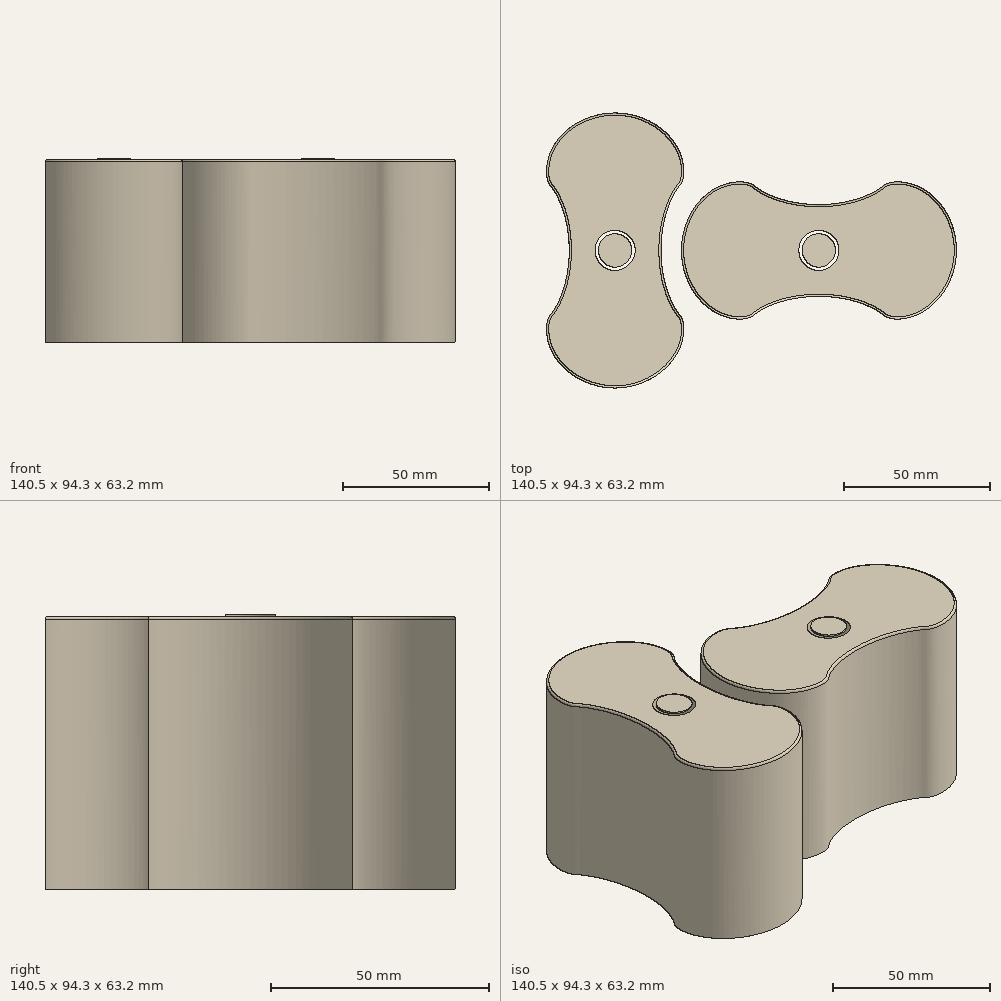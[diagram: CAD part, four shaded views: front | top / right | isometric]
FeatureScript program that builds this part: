
annotation { "Feature Type Name" : "Feature", "Feature Type Description" : "" }
export const myFeature = defineFeature(function(context is Context, id is Id, definition is map)
    precondition{}
    {
        {
            var Q0;
            Q0=qCreatedBy(makeId("Top.planeOp"),FACE);
            var sketch = newSketch(context, id + "F0", { "sketchPlane" : qUnion([Q0])});
            skCircle(sketch, "E0", {"center": v(0, 0) * mm, "radius": 31.43 * mm, "construction": true});
            skCircle(sketch, "E1", {"center": v(0, 39.3) * mm, "radius": 7.86 * mm, "construction": true});
            skLineSegment(sketch, "E2", {"start": v(0, 47.15) * mm, "end": v(0, 39.3) * mm, "construction": true});
            skLineSegment(sketch, "E3", {"start": v(0, 0) * mm, "end": v(-23.57, 0) * mm, "construction": true});
            skCircle(sketch, "E4", {"center": v(-23.57, 0) * mm, "radius": 7.86 * mm, "construction": true});
            skLineSegment(sketch, "E5", {"start": v(0, 0) * mm, "end": v(0, 47.15) * mm, "construction": true});
            skCircle(sketch, "E6", {"center": v(0, 0) * mm, "radius": 47.15 * mm, "construction": true});
            skLineSegment(sketch, "E7", {"start": v(0, 0) * mm, "end": v(-22.23, 22.23) * mm, "construction": true});
            skLineSegment(sketch, "E8", {"start": v(0, 0) * mm, "end": v(0, -47.15) * mm, "construction": true});
            skLineSegment(sketch, "E9", {"start": v(0, 0) * mm, "end": v(-22.23, -22.23) * mm, "construction": true});
            skCircle(sketch, "E10", {"center": v(0, -39.3) * mm, "radius": 7.86 * mm, "construction": true});
            skCircle(sketch, "E11", {"center": v(-15.04, 36.3) * mm, "radius": 7.86 * mm, "construction": true});
            skCircle(sketch, "E12", {"center": v(-21.78, 9.02) * mm, "radius": 7.86 * mm, "construction": true});
            skLineSegment(sketch, "E13", {"start": v(-15.04, 36.3) * mm, "end": v(0, 0) * mm, "construction": true});
            skLineSegment(sketch, "E14", {"start": v(0, 0) * mm, "end": v(-21.78, 9.02) * mm, "construction": true});
            skLineSegment(sketch, "E15", {"start": v(-21.78, 9.02) * mm, "end": v(-18.77, 16.28) * mm, "construction": true});
            skLineSegment(sketch, "E16", {"start": v(-15.04, 36.3) * mm, "end": v(-22.3, 33.3) * mm, "construction": true});
            skPoint(sketch, "E17", {"position": v(-15.72, 0) * mm});
            skCircle(sketch, "E18", {"center": v(-21.78, -9.02) * mm, "radius": 7.86 * mm, "construction": true});
            skCircle(sketch, "E19", {"center": v(-15.04, -36.3) * mm, "radius": 7.86 * mm, "construction": true});
            skLineSegment(sketch, "E20", {"start": v(0, 0) * mm, "end": v(-21.78, -9.02) * mm, "construction": true});
            skLineSegment(sketch, "E21", {"start": v(0, 0) * mm, "end": v(-15.04, -36.3) * mm, "construction": true});
            skLineSegment(sketch, "E22", {"start": v(-21.78, -9.02) * mm, "end": v(-18.77, -16.28) * mm, "construction": true});
            skLineSegment(sketch, "E23", {"start": v(-15.04, -36.3) * mm, "end": v(-22.3, -33.3) * mm, "construction": true});
            skCircle(sketch, "E24", {"center": v(-7.67, 38.54) * mm, "radius": 7.86 * mm, "construction": true});
            skLineSegment(sketch, "E25", {"start": v(-7.67, 38.54) * mm, "end": v(0, 0) * mm, "construction": true});
            skCircle(sketch, "E26", {"center": v(-21.83, 32.67) * mm, "radius": 7.86 * mm, "construction": true});
            skLineSegment(sketch, "E27", {"start": v(-21.83, 32.67) * mm, "end": v(0, 0) * mm, "construction": true});
            skLineSegment(sketch, "E28", {"start": v(-7.67, 38.54) * mm, "end": v(-14.2, 42.9) * mm, "construction": true});
            skLineSegment(sketch, "E29", {"start": v(-21.83, 32.67) * mm, "end": v(-23.36, 24.96) * mm, "construction": true});
            skCircle(sketch, "E30", {"center": v(-19.6, 13.1) * mm, "radius": 7.86 * mm, "construction": true});
            skCircle(sketch, "E31", {"center": v(-23.12, 4.6) * mm, "radius": 7.86 * mm, "construction": true});
            skLineSegment(sketch, "E32", {"start": v(-19.6, 13.1) * mm, "end": v(0, 0) * mm, "construction": true});
            skLineSegment(sketch, "E33", {"start": v(-19.6, 13.1) * mm, "end": v(-21.13, 20.8) * mm, "construction": true});
            skLineSegment(sketch, "E34", {"start": v(-23.12, 4.6) * mm, "end": v(0, 0) * mm, "construction": true});
            skLineSegment(sketch, "E35", {"start": v(-23.12, 4.6) * mm, "end": v(-16.59, 8.96) * mm, "construction": true});
            skCircle(sketch, "E36", {"center": v(-23.12, -4.6) * mm, "radius": 7.86 * mm, "construction": true});
            skLineSegment(sketch, "E37", {"start": v(-23.12, -4.6) * mm, "end": v(0, 0) * mm, "construction": true});
            skLineSegment(sketch, "E38", {"start": v(-23.12, -4.6) * mm, "end": v(-16.59, -8.96) * mm, "construction": true});
            skCircle(sketch, "E39", {"center": v(-19.6, -13.1) * mm, "radius": 7.86 * mm, "construction": true});
            skCircle(sketch, "E40", {"center": v(-21.83, -32.67) * mm, "radius": 7.86 * mm, "construction": true});
            skCircle(sketch, "E41", {"center": v(-7.67, -38.54) * mm, "radius": 7.86 * mm, "construction": true});
            skLineSegment(sketch, "E42", {"start": v(-19.6, -13.1) * mm, "end": v(0, 0) * mm, "construction": true});
            skLineSegment(sketch, "E43", {"start": v(-19.6, -13.1) * mm, "end": v(-21.13, -20.8) * mm, "construction": true});
            skLineSegment(sketch, "E44", {"start": v(-21.83, -32.67) * mm, "end": v(0, 0) * mm, "construction": true});
            skLineSegment(sketch, "E45", {"start": v(-7.67, -38.54) * mm, "end": v(0, 0) * mm, "construction": true});
            skLineSegment(sketch, "E46", {"start": v(-21.83, -32.67) * mm, "end": v(-23.36, -24.96) * mm, "construction": true});
            skLineSegment(sketch, "E47", {"start": v(-7.67, -38.54) * mm, "end": v(-14.2, -42.9) * mm, "construction": true});
            skSolve(sketch);
        }
        {
            var Q0;
            Q0=qCreatedBy(makeId("Top.planeOp"),FACE);
            var sketch = newSketch(context, id + "F1", { "sketchPlane" : qUnion([Q0])});
            skPoint(sketch, "E48.0", {"position": v(0, 47.15) * mm});
            skPoint(sketch, "E48.1", {"position": v(-14.2, 42.9) * mm});
            skPoint(sketch, "E48.2", {"position": v(-22.3, 33.3) * mm});
            skPoint(sketch, "E48.3", {"position": v(-23.36, 24.96) * mm});
            skPoint(sketch, "E48.4", {"position": v(-22.23, 22.23) * mm});
            skPoint(sketch, "E48.5", {"position": v(-21.13, 20.8) * mm});
            skPoint(sketch, "E48.6", {"position": v(-18.77, 16.28) * mm});
            skPoint(sketch, "E48.7", {"position": v(-16.59, 8.96) * mm});
            skPoint(sketch, "E48.8", {"position": v(-15.72, 0) * mm});
            skPoint(sketch, "E48.9", {"position": v(-16.59, -8.96) * mm});
            skPoint(sketch, "E48.10", {"position": v(-18.77, -16.28) * mm});
            skPoint(sketch, "E48.11", {"position": v(-21.13, -20.8) * mm});
            skPoint(sketch, "E48.12", {"position": v(-22.23, -22.23) * mm});
            skPoint(sketch, "E48.13", {"position": v(-23.36, -24.96) * mm});
            skPoint(sketch, "E48.14", {"position": v(-22.3, -33.3) * mm});
            skPoint(sketch, "E48.15", {"position": v(-14.2, -42.9) * mm});
            skPoint(sketch, "E49.1.0", {"position": v(16.59, -8.96) * mm});
            skPoint(sketch, "E49.1.1", {"position": v(16.59, 8.96) * mm});
            skPoint(sketch, "E49.1.2", {"position": v(15.72, 0) * mm});
            skPoint(sketch, "E49.1.3", {"position": v(23.36, 24.96) * mm});
            skPoint(sketch, "E49.1.4", {"position": v(22.3, 33.3) * mm});
            skPoint(sketch, "E49.1.5", {"position": v(18.77, 16.28) * mm});
            skPoint(sketch, "E49.1.6", {"position": v(21.13, 20.8) * mm});
            skPoint(sketch, "E49.1.7", {"position": v(22.23, 22.23) * mm});
            skPoint(sketch, "E49.1.8", {"position": v(14.2, 42.9) * mm});
            skPoint(sketch, "E49.1.9", {"position": v(0, -47.15) * mm});
            skPoint(sketch, "E49.1.10", {"position": v(22.3, -33.3) * mm});
            skPoint(sketch, "E49.1.11", {"position": v(14.2, -42.9) * mm});
            skPoint(sketch, "E49.1.12", {"position": v(23.36, -24.96) * mm});
            skPoint(sketch, "E49.1.13", {"position": v(22.23, -22.23) * mm});
            skPoint(sketch, "E49.1.14", {"position": v(21.13, -20.8) * mm});
            skPoint(sketch, "E49.1.15", {"position": v(18.77, -16.28) * mm});
            skPoint(sketch, "E49.center", {"position": v(0, 0) * mm});
            skFitSpline(sketch, "E50", {"points": [v(0, 47.15) * mm, v(-14.2, 42.9) * mm, v(-22.3, 33.3) * mm, v(-23.36, 24.96) * mm, v(-22.23, 22.23) * mm, v(-21.13, 20.8) * mm, v(-18.77, 16.28) * mm, v(-16.59, 8.96) * mm, v(-15.72, 0) * mm, v(-16.59, -8.96) * mm, v(-18.77, -16.28) * mm, v(-21.13, -20.8) * mm, v(-22.23, -22.23) * mm, v(-23.36, -24.96) * mm, v(-22.3, -33.3) * mm, v(-14.2, -42.9) * mm, v(0, -47.15) * mm, v(14.2, -42.9) * mm, v(22.3, -33.3) * mm, v(23.36, -24.96) * mm, v(22.23, -22.23) * mm, v(21.13, -20.8) * mm, v(18.77, -16.28) * mm, v(16.59, -8.96) * mm, v(15.72, 0) * mm, v(16.59, 8.96) * mm, v(18.77, 16.28) * mm, v(21.13, 20.8) * mm, v(22.23, 22.23) * mm, v(23.36, 24.96) * mm, v(22.3, 33.3) * mm, v(14.2, 42.9) * mm, v(0, 47.15) * mm]});
            skCircle(sketch, "E51", {"center": v(0, 0) * mm, "radius": 4.38 * mm, "construction": true});
            skLineSegment(sketch, "E52", {"start": v(3.7, -2.33) * mm, "end": v(-3.7, -2.33) * mm, "construction": true});
            skLineSegment(sketch, "E53", {"start": v(0, 4.38) * mm, "end": v(-8.21, 4.38) * mm, "construction": true});
            skFitSpline(sketch, "E54.0", {"points": [v(2.38, 44.66) * mm, v(0, 44.79) * mm, v(-2.38, 44.66) * mm, v(-5.53, 44.17) * mm, v(-8.58, 43.2) * mm, v(-11.38, 41.84) * mm, v(-13.97, 40.23) * mm, v(-16.22, 38.26) * mm, v(-18.03, 36.07) * mm, v(-18.96, 34.63) * mm, v(-19.58, 33.45) * mm, v(-19.98, 32.56) * mm, v(-20.3, 31.66) * mm, v(-20.67, 30.45) * mm, v(-20.97, 28.95) * mm, v(-21.09, 27.55) * mm, v(-21.08, 26.56) * mm, v(-21.03, 26.01) * mm, v(-20.98, 25.63) * mm, v(-20.92, 25.29) * mm, v(-20.79, 24.77) * mm, v(-20.6, 24.32) * mm, v(-20.4, 23.95) * mm, v(-20.23, 23.7) * mm, v(-20.05, 23.47) * mm, v(-19.8, 23.18) * mm, v(-19.55, 22.85) * mm, v(-19.3, 22.53) * mm, v(-19.12, 22.26) * mm, v(-18.92, 21.98) * mm, v(-18.67, 21.58) * mm, v(-18.34, 21.04) * mm, v(-17.95, 20.33) * mm, v(-17.42, 19.32) * mm, v(-16.9, 18.22) * mm, v(-16.4, 17.05) * mm, v(-15.7, 15.27) * mm, v(-14.8, 12.48) * mm, v(-13.93, 8.5) * mm, v(-13.38, 4.31) * mm, v(-13.18, 0) * mm, v(-13.38, -4.31) * mm, v(-13.93, -8.5) * mm, v(-14.8, -12.48) * mm, v(-15.7, -15.27) * mm, v(-16.4, -17.05) * mm, v(-16.9, -18.22) * mm, v(-17.42, -19.32) * mm, v(-17.95, -20.33) * mm, v(-18.34, -21.04) * mm, v(-18.67, -21.58) * mm, v(-18.92, -21.98) * mm, v(-19.12, -22.26) * mm, v(-19.3, -22.53) * mm, v(-19.55, -22.85) * mm, v(-19.8, -23.18) * mm, v(-20.05, -23.47) * mm, v(-20.23, -23.7) * mm, v(-20.4, -23.95) * mm, v(-20.6, -24.32) * mm, v(-20.79, -24.77) * mm, v(-20.92, -25.29) * mm, v(-20.98, -25.63) * mm, v(-21.03, -26.01) * mm, v(-21.08, -26.56) * mm, v(-21.09, -27.55) * mm, v(-20.97, -28.95) * mm, v(-20.67, -30.45) * mm, v(-20.3, -31.66) * mm, v(-19.98, -32.56) * mm, v(-19.58, -33.45) * mm, v(-18.96, -34.63) * mm, v(-18.03, -36.07) * mm, v(-16.22, -38.26) * mm, v(-13.97, -40.23) * mm, v(-11.38, -41.84) * mm, v(-8.58, -43.2) * mm, v(-5.53, -44.17) * mm, v(-2.38, -44.66) * mm, v(0, -44.79) * mm, v(2.38, -44.66) * mm, v(5.53, -44.17) * mm, v(8.58, -43.2) * mm, v(11.38, -41.84) * mm, v(13.97, -40.23) * mm, v(16.22, -38.26) * mm, v(18.03, -36.07) * mm, v(18.96, -34.63) * mm, v(19.58, -33.45) * mm, v(19.98, -32.56) * mm, v(20.3, -31.66) * mm, v(20.67, -30.45) * mm, v(20.97, -28.95) * mm, v(21.09, -27.55) * mm, v(21.08, -26.56) * mm, v(21.03, -26.01) * mm, v(20.98, -25.63) * mm, v(20.92, -25.29) * mm, v(20.79, -24.77) * mm, v(20.6, -24.32) * mm, v(20.4, -23.95) * mm, v(20.23, -23.7) * mm, v(20.05, -23.47) * mm, v(19.8, -23.18) * mm, v(19.55, -22.85) * mm, v(19.3, -22.53) * mm, v(19.12, -22.26) * mm, v(18.92, -21.98) * mm, v(18.67, -21.58) * mm, v(18.34, -21.04) * mm, v(17.95, -20.33) * mm, v(17.42, -19.32) * mm, v(16.9, -18.22) * mm, v(16.4, -17.05) * mm, v(15.7, -15.27) * mm, v(14.8, -12.48) * mm, v(13.93, -8.5) * mm, v(13.38, -4.31) * mm, v(13.18, 0) * mm, v(13.38, 4.31) * mm, v(13.93, 8.5) * mm, v(14.8, 12.48) * mm, v(15.7, 15.27) * mm, v(16.4, 17.05) * mm, v(16.9, 18.22) * mm, v(17.42, 19.32) * mm, v(17.95, 20.33) * mm, v(18.34, 21.04) * mm, v(18.67, 21.58) * mm, v(18.92, 21.98) * mm, v(19.12, 22.26) * mm, v(19.3, 22.53) * mm, v(19.55, 22.85) * mm, v(19.8, 23.18) * mm, v(20.05, 23.47) * mm, v(20.23, 23.7) * mm, v(20.4, 23.95) * mm, v(20.6, 24.32) * mm, v(20.79, 24.77) * mm, v(20.92, 25.29) * mm, v(20.98, 25.63) * mm, v(21.03, 26.01) * mm, v(21.08, 26.56) * mm, v(21.09, 27.55) * mm, v(20.97, 28.95) * mm, v(20.67, 30.45) * mm, v(20.3, 31.66) * mm, v(19.98, 32.56) * mm, v(19.58, 33.45) * mm, v(18.96, 34.63) * mm, v(18.03, 36.07) * mm, v(16.22, 38.26) * mm, v(13.97, 40.23) * mm, v(11.38, 41.84) * mm, v(8.58, 43.2) * mm, v(5.53, 44.17) * mm, v(2.38, 44.66) * mm, v(0, 44.79) * mm, v(-2.38, 44.66) * mm, v(2.38, 44.66) * mm]});
            skCircle(sketch, "E55", {"center": v(0, 0) * mm, "radius": 6.88 * mm});
            skLineSegment(sketch, "E56", {"start": v(0, 6.88) * mm, "end": v(-13.7, 6.88) * mm});
            skLineSegment(sketch, "E57", {"start": v(0, 6.88) * mm, "end": v(13.7, 6.88) * mm});
            skLineSegment(sketch, "E58", {"start": v(0, -6.88) * mm, "end": v(13.7, -6.88) * mm});
            skLineSegment(sketch, "E59", {"start": v(0, -6.88) * mm, "end": v(-13.7, -6.88) * mm});
            skSolve(sketch);
        }
        {
            var Q0;
            Q0=makeQuery(id+"F1.imprint","IMPRINT",FACE,{"disambiguationData":[TD([[makeQuery(id+"F1.imprint","IMPRINT",EDGE,{"derivedFrom":sQuery(id+"F1.wireOp",EDGE,"E50")}),1.0]])]});
            var Q1;
            {var subQ0=sQuery(id+"F1.wireOp",EDGE,"E56");Q1=makeQuery(id+"F1.imprint","IMPRINT",FACE,{"disambiguationData":[TD([[makeQuery(id+"F1.imprint","IMPRINT",EDGE,{"derivedFrom":subQ0}),1.0]])]});}
            var Q2;
            {var subQ0=sQuery(id+"F1.wireOp",EDGE,"E57");Q2=makeQuery(id+"F1.imprint","IMPRINT",FACE,{"disambiguationData":[TD([[makeQuery(id+"F1.imprint","IMPRINT",EDGE,{"derivedFrom":subQ0}),-1.0]])]});}
            var Q3;
            {var subQ0=sQuery(id+"F1.wireOp",EDGE,"E52");var subQ1=sQuery(id+"F1.wireOp",EDGE,"E51");var subQ2=makeQuery(id+"F1.imprint","INTERSECT",VERTEX,{"disambiguationData":[OD(0.0)],"derivedFrom":[subQ1,subQ0]});Q3=makeQuery(id+"F1.imprint","IMPRINT",FACE,{"disambiguationData":[TD([[makeQuery(id+"F1.imprint","IMPRINT",EDGE,{"disambiguationData":[TD([[subQ2,1.0]])],"derivedFrom":subQ1}),-1.0]])]});}
            var Q4;
            {var subQ0=sQuery(id+"F1.wireOp",EDGE,"E52");Q4=makeQuery(id+"F1.imprint","IMPRINT",FACE,{"disambiguationData":[TD([[makeQuery(id+"F1.imprint","IMPRINT",EDGE,{"derivedFrom":subQ0}),1.0]])]});}
            var Q5;
            {var subQ0=sQuery(id+"F1.wireOp",EDGE,"E55");var subQ1=makeQuery(id+"F1.imprint","INTERSECT",VERTEX,{"derivedFrom":[subQ0,sQuery(id+"F1.wireOp",EDGE,"E56"),sQuery(id+"F1.wireOp",EDGE,"E57")]});Q5=makeQuery(id+"F1.imprint","IMPRINT",FACE,{"disambiguationData":[TD([[makeQuery(id+"F1.imprint","IMPRINT",EDGE,{"disambiguationData":[TD([[subQ1,-1.0]])],"derivedFrom":subQ0}),1.0]])]});}
            extrude(context, id + "F2", {"entities" : qUnion([Q0, Q1, Q2, Q3, Q4, Q5]), "depth" : 62.74 * mm, "offsetDistance" : 25.4 * mm});
        }
        {
            var Q0;
            Q0=makeQuery(id+"F2.opExtrude","SWEPT_BODY",BODY,{"disambiguationData":[OSD([sQuery(id+"F1.wireOp",EDGE,"E50"),sQuery(id+"F1.wireOp",EDGE,"E54.0"),sQuery(id+"F1.wireOp",EDGE,"E56"),sQuery(id+"F1.wireOp",EDGE,"E57"),sQuery(id+"F1.wireOp",EDGE,"E58"),sQuery(id+"F1.wireOp",EDGE,"E59")])]});
            transform(context, id + "F3", {"entities" : qUnion([Q0]), "transformType" : TransformType.TRANSLATION_3D, "dx" : 69.85 * mm, "dy" : 0 * mm, "dz" : 0 * mm, "makeCopy" : true});
        }
        {
            var Q0;
            Q0=makeQuery(id+"F3.opPattern","COPY",FACE,{"derivedFrom":makeQuery(id+"F2.opExtrude","CAP_FACE",FACE,{"disambiguationData":[OSD([sQuery(id+"F1.wireOp",EDGE,"E50"),sQuery(id+"F1.wireOp",EDGE,"E54.0"),sQuery(id+"F1.wireOp",EDGE,"E56"),sQuery(id+"F1.wireOp",EDGE,"E57"),sQuery(id+"F1.wireOp",EDGE,"E58"),sQuery(id+"F1.wireOp",EDGE,"E59")])],"isStart":false}),"instanceName":"1"});
            var sketch = newSketch(context, id + "F4", { "sketchPlane" : qUnion([Q0])});
            skLineSegment(sketch, "E60", {"start": v(69.85, 6.88) * mm, "end": v(69.85, -6.88) * mm, "construction": true});
            skCircle(sketch, "E61", {"center": v(69.85, 0) * mm, "radius": 4.25 * mm});
            skSolve(sketch);
        }
        {
            var Q0;
            Q0=makeQuery(id+"F3.opPattern","COPY",BODY,{"derivedFrom":makeQuery(id+"F2.opExtrude","SWEPT_BODY",BODY,{"disambiguationData":[OSD([sQuery(id+"F1.wireOp",EDGE,"E50"),sQuery(id+"F1.wireOp",EDGE,"E54.0"),sQuery(id+"F1.wireOp",EDGE,"E56"),sQuery(id+"F1.wireOp",EDGE,"E57"),sQuery(id+"F1.wireOp",EDGE,"E58"),sQuery(id+"F1.wireOp",EDGE,"E59")])]}),"instanceName":"1"});
            var Q1;
            Q1=sQuery(id+"F4.wireOp",EDGE,"E61");
            transform(context, id + "F5", {"entities" : qUnion([Q0]), "transformType" : TransformType.ROTATION, "transformAxis" : qUnion([Q1]), "angle" : 90 * degree, "makeCopy" : false});
        }
        {
            var Q0;
            Q0=makeQuery(id+"F2.opExtrude","CAP_FACE",FACE,{"disambiguationData":[OSD([sQuery(id+"F1.wireOp",EDGE,"E50"),sQuery(id+"F1.wireOp",EDGE,"E54.0"),sQuery(id+"F1.wireOp",EDGE,"E56"),sQuery(id+"F1.wireOp",EDGE,"E57"),sQuery(id+"F1.wireOp",EDGE,"E58"),sQuery(id+"F1.wireOp",EDGE,"E59")])],"isStart":false});
            var sketch = newSketch(context, id + "F6", { "sketchPlane" : qUnion([Q0])});
            skCircle(sketch, "E62", {"center": v(0, 0) * mm, "radius": 4.25 * mm});
            skLineSegment(sketch, "E63", {"start": v(2.4, 3.51) * mm, "end": v(2.4, -3.51) * mm});
            skSolve(sketch);
        }
        {
            var Q0;
            {var subQ0=sQuery(id+"F6.wireOp",EDGE,"E63");Q0=makeQuery(id+"F6.imprint","IMPRINT",FACE,{"disambiguationData":[TD([[makeQuery(id+"F6.imprint","IMPRINT",EDGE,{"derivedFrom":subQ0}),-1.0]])]});}
            extrude(context, id + "F7", {"entities" : qUnion([Q0]), "operationType" : NewBodyOperationType.REMOVE, "endBound" : BoundingType.THROUGH_ALL, "oppositeDirection" : true, "depth" : 25.4 * mm, "offsetDistance" : 25.4 * mm});
        }
        {
            var Q0;
            Q0=makeQuery(id+"F3.opPattern","COPY",FACE,{"derivedFrom":makeQuery(id+"F2.opExtrude","CAP_FACE",FACE,{"disambiguationData":[OSD([sQuery(id+"F1.wireOp",EDGE,"E50"),sQuery(id+"F1.wireOp",EDGE,"E54.0"),sQuery(id+"F1.wireOp",EDGE,"E56"),sQuery(id+"F1.wireOp",EDGE,"E57"),sQuery(id+"F1.wireOp",EDGE,"E58"),sQuery(id+"F1.wireOp",EDGE,"E59")])],"isStart":false}),"instanceName":"1"});
            var sketch = newSketch(context, id + "F8", { "sketchPlane" : qUnion([Q0])});
            skLineSegment(sketch, "E64", {"start": v(62.97, 0) * mm, "end": v(76.73, 0) * mm, "construction": true});
            skCircle(sketch, "E65", {"center": v(69.85, 0) * mm, "radius": 4.25 * mm});
            skLineSegment(sketch, "E66", {"start": v(67.45, 3.51) * mm, "end": v(67.45, -3.51) * mm});
            skSolve(sketch);
        }
        {
            var Q0;
            {var subQ0=sQuery(id+"F8.wireOp",EDGE,"E66");Q0=makeQuery(id+"F8.imprint","IMPRINT",FACE,{"disambiguationData":[TD([[makeQuery(id+"F8.imprint","IMPRINT",EDGE,{"derivedFrom":subQ0}),1.0]])]});}
            extrude(context, id + "F9", {"entities" : qUnion([Q0]), "operationType" : NewBodyOperationType.REMOVE, "endBound" : BoundingType.THROUGH_ALL, "oppositeDirection" : true, "depth" : 25.4 * mm, "offsetDistance" : 25.4 * mm});
        }
        {
            var Q0;
            Q0=makeQuery(id+"F2.opExtrude","CAP_FACE",FACE,{"disambiguationData":[OSD([sQuery(id+"F1.wireOp",EDGE,"E50"),sQuery(id+"F1.wireOp",EDGE,"E54.0"),sQuery(id+"F1.wireOp",EDGE,"E56"),sQuery(id+"F1.wireOp",EDGE,"E57"),sQuery(id+"F1.wireOp",EDGE,"E58"),sQuery(id+"F1.wireOp",EDGE,"E59")])],"isStart":false});
            var sketch = newSketch(context, id + "F10", { "sketchPlane" : qUnion([Q0])});
            skCircle(sketch, "E67", {"center": v(0, 0) * mm, "radius": 5.72 * mm});
            skSolve(sketch);
        }
        {
            var Q0;
            Q0=makeQuery(id+"F10.imprint","IMPRINT",FACE,{"disambiguationData":[TD([[makeQuery(id+"F10.imprint","IMPRINT",EDGE,{"derivedFrom":sQuery(id+"F10.wireOp",EDGE,"E67")}),1.0]])]});
            extrude(context, id + "F11", {"entities" : qUnion([Q0]), "operationType" : NewBodyOperationType.ADD, "depth" : 0.5 * mm, "offsetDistance" : 25.4 * mm});
        }
        {
            var Q0;
            Q0=makeQuery(id+"F3.opPattern","COPY",FACE,{"derivedFrom":makeQuery(id+"F2.opExtrude","CAP_FACE",FACE,{"disambiguationData":[OSD([sQuery(id+"F1.wireOp",EDGE,"E50"),sQuery(id+"F1.wireOp",EDGE,"E54.0"),sQuery(id+"F1.wireOp",EDGE,"E56"),sQuery(id+"F1.wireOp",EDGE,"E57"),sQuery(id+"F1.wireOp",EDGE,"E58"),sQuery(id+"F1.wireOp",EDGE,"E59")])],"isStart":false}),"instanceName":"1"});
            var sketch = newSketch(context, id + "F12", { "sketchPlane" : qUnion([Q0])});
            skCircle(sketch, "E68", {"center": v(69.85, 0) * mm, "radius": 5.72 * mm});
            skSolve(sketch);
        }
        {
            var Q0;
            Q0=makeQuery(id+"F12.imprint","IMPRINT",FACE,{"disambiguationData":[TD([[makeQuery(id+"F12.imprint","IMPRINT",EDGE,{"derivedFrom":sQuery(id+"F12.wireOp",EDGE,"E68")}),1.0]])]});
            extrude(context, id + "F13", {"entities" : qUnion([Q0]), "operationType" : NewBodyOperationType.ADD, "depth" : 0.5 * mm, "offsetDistance" : 25.4 * mm});
        }
        {
            var Q0;
            Q0=makeQuery(id+"F2.opExtrude","CAP_EDGE",EDGE,{"disambiguationData":[OSD([sQuery(id+"F1.wireOp",EDGE,"E50")])],"isStart":false});
            var Q1;
            Q1=makeQuery(id+"F3.opPattern","COPY",EDGE,{"derivedFrom":makeQuery(id+"F2.opExtrude","CAP_EDGE",EDGE,{"disambiguationData":[OSD([sQuery(id+"F1.wireOp",EDGE,"E50")])],"isStart":false}),"instanceName":"1"});
            var Q2;
            Q2=makeQuery(id+"F9.boolean.opBoolean","COPY",EDGE,{"derivedFrom":makeQuery(id+"F9.opExtrude","CAP_EDGE",EDGE,{"disambiguationData":[OSD([sQuery(id+"F8.wireOp",EDGE,"E65")])],"isStart":true})});
            var Q3;
            Q3=makeQuery(id+"F9.boolean.opBoolean","COPY",EDGE,{"derivedFrom":makeQuery(id+"F9.opExtrude","CAP_EDGE",EDGE,{"disambiguationData":[OSD([sQuery(id+"F8.wireOp",EDGE,"E66")])],"isStart":true})});
            var Q4;
            {var subQ0=sQuery(id+"F1.wireOp",EDGE,"E54.0");Q4=makeQuery(id+"F3.opPattern","COPY",EDGE,{"derivedFrom":makeQuery(id+"F2.opExtrude","CAP_EDGE",EDGE,{"disambiguationData":[OSD([subQ0]),TDD([makeQuery(id+"F1.imprint","IMPRINT",EDGE,{"disambiguationData":[TD([[makeQuery(id+"F1.imprint","INTERSECT",VERTEX,{"derivedFrom":[subQ0,sQuery(id+"F1.wireOp",EDGE,"E56")]}),1.0]])],"derivedFrom":subQ0})])],"isStart":false}),"instanceName":"1"});}
            var Q5;
            {var subQ0=sQuery(id+"F1.wireOp",EDGE,"E54.0");Q5=makeQuery(id+"F3.opPattern","COPY",EDGE,{"derivedFrom":makeQuery(id+"F2.opExtrude","CAP_EDGE",EDGE,{"disambiguationData":[OSD([subQ0]),TDD([makeQuery(id+"F1.imprint","IMPRINT",EDGE,{"disambiguationData":[TD([[makeQuery(id+"F1.imprint","INTERSECT",VERTEX,{"derivedFrom":[subQ0,sQuery(id+"F1.wireOp",EDGE,"E58")]}),1.0]])],"derivedFrom":subQ0})])],"isStart":false}),"instanceName":"1"});}
            var Q6;
            {var subQ0=sQuery(id+"F1.wireOp",EDGE,"E54.0");Q6=makeQuery(id+"F2.opExtrude","CAP_EDGE",EDGE,{"disambiguationData":[OSD([subQ0]),TDD([makeQuery(id+"F1.imprint","IMPRINT",EDGE,{"disambiguationData":[TD([[makeQuery(id+"F1.imprint","INTERSECT",VERTEX,{"derivedFrom":[subQ0,sQuery(id+"F1.wireOp",EDGE,"E58")]}),1.0]])],"derivedFrom":subQ0})])],"isStart":false});}
            var Q7;
            {var subQ0=sQuery(id+"F1.wireOp",EDGE,"E54.0");Q7=makeQuery(id+"F2.opExtrude","CAP_EDGE",EDGE,{"disambiguationData":[OSD([subQ0]),TDD([makeQuery(id+"F1.imprint","IMPRINT",EDGE,{"disambiguationData":[TD([[makeQuery(id+"F1.imprint","INTERSECT",VERTEX,{"derivedFrom":[subQ0,sQuery(id+"F1.wireOp",EDGE,"E56")]}),1.0]])],"derivedFrom":subQ0})])],"isStart":false});}
            var Q8;
            Q8=makeQuery(id+"F2.opExtrude","CAP_EDGE",EDGE,{"disambiguationData":[OSD([sQuery(id+"F1.wireOp",EDGE,"E58"),sQuery(id+"F1.wireOp",EDGE,"E59")])],"isStart":false});
            var Q9;
            Q9=makeQuery(id+"F2.opExtrude","CAP_EDGE",EDGE,{"disambiguationData":[OSD([sQuery(id+"F1.wireOp",EDGE,"E56"),sQuery(id+"F1.wireOp",EDGE,"E57")])],"isStart":false});
            var Q10;
            Q10=makeQuery(id+"F3.opPattern","COPY",EDGE,{"derivedFrom":makeQuery(id+"F2.opExtrude","CAP_EDGE",EDGE,{"disambiguationData":[OSD([sQuery(id+"F1.wireOp",EDGE,"E56"),sQuery(id+"F1.wireOp",EDGE,"E57")])],"isStart":false}),"instanceName":"1"});
            var Q11;
            Q11=makeQuery(id+"F3.opPattern","COPY",EDGE,{"derivedFrom":makeQuery(id+"F2.opExtrude","CAP_EDGE",EDGE,{"disambiguationData":[OSD([sQuery(id+"F1.wireOp",EDGE,"E58"),sQuery(id+"F1.wireOp",EDGE,"E59")])],"isStart":false}),"instanceName":"1"});
            var Q12;
            Q12=makeQuery(id+"F7.boolean.opBoolean","COPY",EDGE,{"derivedFrom":makeQuery(id+"F7.opExtrude","CAP_EDGE",EDGE,{"disambiguationData":[OSD([sQuery(id+"F6.wireOp",EDGE,"E62")])],"isStart":true})});
            var Q13;
            Q13=makeQuery(id+"F7.boolean.opBoolean","COPY",EDGE,{"derivedFrom":makeQuery(id+"F7.opExtrude","CAP_EDGE",EDGE,{"disambiguationData":[OSD([sQuery(id+"F6.wireOp",EDGE,"E63")])],"isStart":true})});
            var Q14;
            Q14=makeQuery(id+"F11.opExtrude","CAP_EDGE",EDGE,{"disambiguationData":[OSD([sQuery(id+"F6.wireOp",EDGE,"E62")])],"isStart":false});
            var Q15;
            Q15=makeQuery(id+"F11.opExtrude","CAP_EDGE",EDGE,{"disambiguationData":[OSD([sQuery(id+"F6.wireOp",EDGE,"E63")])],"isStart":false});
            var Q16;
            Q16=makeQuery(id+"F13.opExtrude","CAP_EDGE",EDGE,{"disambiguationData":[OSD([sQuery(id+"F8.wireOp",EDGE,"E65")])],"isStart":false});
            var Q17;
            Q17=makeQuery(id+"F13.opExtrude","CAP_EDGE",EDGE,{"disambiguationData":[OSD([sQuery(id+"F8.wireOp",EDGE,"E66")])],"isStart":false});
            fillet(context, id + "F14", {"entities" : qUnion([Q0, Q1, Q2, Q3, Q4, Q5, Q6, Q7, Q8, Q9, Q10, Q11, Q12, Q13, Q14, Q15, Q16, Q17]), "radius" : 0.76 * mm, "tangentPropagation" : true, "allowEdgeOverflow" : false});
        }
    });
